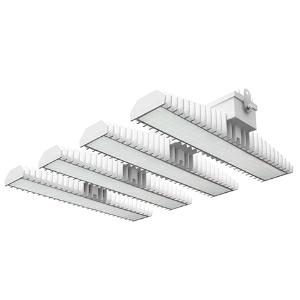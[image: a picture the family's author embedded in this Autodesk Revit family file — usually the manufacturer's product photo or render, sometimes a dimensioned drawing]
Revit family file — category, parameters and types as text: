
# Revit family: 3f_filippi_-_3f_lem_ho_ampio_3f_filippi_-_58956_a0812_-_3f_lem_4_ho_led_280_cr_ampio___vs_26d4
name_source: partatom
category: Lighting Fixtures
units: mm (PartAtom-declared; Revit-internal decimal feet)

## family parameters
Cut with Voids When Loaded = No
Host = Face
Light Source = No
Part Type = Normal
Room Calculation Point = No
Round Connector Dimension = Use Diameter
Shared = No

## types (1)
- 3F Filippi - 3F LEM HO Ampio (1 x LED, 35405 lm, 276 W, 4000 K)
    Apparent Load = 276 VA
    Approval mark = CE
    CIE Flux Codes = 67 90 97 100 100
    Color Rendering = 80
    Color Temperature = 4000 K
    Control Gear = Electronic ballast
    Default Elevation = 1800 mm
    Description = Industrial luminaire with high light output and high luminous efficiency designed with the most innovative technologies for environments with temperature up to 55°C.

ILLUMINOTECHNICAL
Luminous efficiency 100% (DLOR 98%, ULOR 2%).
Initial luminous flux of the luminaire 35405 lm.
Direct symmetric wide distribution: the illuminated area has a rectangular shape.
Installation Interdistance Transv.D = 1.24 x hu - Long.D = 1.20 x hu.
Tabular UGR (CIE 117 - 4H-8H; S=0.25H; 70/50/20): RUG 23.8 - 23.9.
Beam angle: 82° - 83°.
Luminous efficacy 128 lm/W.
Lifetime (L93/B10): 30000 h. (tq+25°C)
Lifetime (L90/B10): 50000 h. (tq+25°C)
Lifetime (L85/B10): 80000 h. (tq+25°C)
Lifetime (L80/B10): 100000 h. (tq+25°C)
Lifetime (L85/B10): 50000 h. (tq+55°C)
Sudden decreased luminous flux after 50000 hours: 0% (C0).
Photobiological safety in compliance with IEC/TR 62778: RG0 risk exempt, (IEC 62471).
In compliance with IEC/EN 62722-2-1 - IEC/EN 62717 standards.

SOURCE
4 Mid-Power linear LED modules 70W/840.
Energy efficiency class (UE 2019/2020 - UE 2019/2015): C.
CIE 13.3 Colour rendering index: CRI >80 (R9 <50%).
IES TM-30 Fidelity Index: Rf = 84 Rg = 95.
CCT nominal colour temperature 4000 K.
Colour initial tolerance (MacAdam): SDCM 3.

MECHANICAL
Passive modular heatsinks in die-casted aluminium, painted in white colour.
To optimize the thermal management of the LED module, the heatsinks are oversized and provided with self-cleaning of cooling fins.
Wiring body in aluminium and galvanised steel anchored solidly to the sinks and thermally separated.
3F Lens lenses with high luminous efficiency, transparent methacrylate (PMMA), fixed to the LED modules.
Fixing brackets in stainless steel.
Luminaire with limited surface temperature. - D - (EN 60598-2-24)
Dimensions: 757x542 mm, height 133 mm. Weight 19.325 kg.
IP65 protection degree.
Mechanical strength to impacts IK06 (1 joule).
Glow-wire test resistance 650°C.

ELECTRICAL
Halogen Free electronic wiring 230V-50/60Hz, power factor 0.97, THD <25%, constant output current, class I, 2 driver.
Power of the luminaire 276 W.
ENEC - CE.
SAFE FLICKER: PstLM=<1 and SVM=<0.4 (IEC TR 61547-1 and IEC TR 63158), to ensure a more comfortable and safe light.
Luminaire compliant with EN 60598-2-22 for power supply from a centralised emergency system CPSS (Central Power Supply System), not incorporated in the luminaire - high risk areas excluded. The default power and flux are 100% in AC and 100% in DC.
Ambient temperature from -30°C to +55°C.
Temperature class T6 max 85°C.
Quick connection via M20 3P connector with 9-13 mm tightening range.
Power unit positioned on a separate compartment by the LED module to ensure optimum temperatures of cabling components, to be inspectable and maintainable.
Relative humidity UR: <85%.

INSTALLATION
Ceiling / Suspended / Wall.
All accessories dedicated to this product are available on the Catalog and on our website www.3F-Filippi.com.

ACCESSORIES
A0812 - Anti-glare microprismatic VS moulded glass, tempered, not flammable, with sealing gasket.
One required for each light module. The pack contains 10 pieces.

APPLICATIONS
In commercial environments, exhibition and industrial areas, stores, open areas.
Environments in which it is necessary a total protection against falling fragments (eg environments with foodstuffs or machines with moving parts or with extreme temperature changes), use luminaires with polycarbonate lenses.

WARNING
Fixture not suitable for cold stores with an ambient temperature <0°C and/or relative humidity >85%.
Luminaire designed for disposal/recycling at end-of-life.
Replaceable (LED only) light source by a professional. Replaceable control gear by a professional.
    Height = 133 mm  [stored 0.436352 ft]
    Lamp = 1 x LED
    Lamp Light Flux = 35405 lm
    Lamp Power = 276 W
    Lamp count = 1
    Length = 757 mm
    Lifetime = 50000 h
    Luminous efficacy = 128 lm/W
    Manufacturer = 3F Filippi
    ModVariant = No
    Model = 3F Filippi - 58956+A0812 - 3F LEM 4 HO LED 280 CR AMPIO + VS
    Mounting Place = Ceiling
    Mounting Type = Pendant
    Number of Poles = 1
    OnlyDefault = Yes
    Power Factor = 1
    Product Name = 3F Filippi - 3F LEM HO Ampio
    Product group = pendant luminaire
    ProductGroupID = 9
    Protection Class = Protection class I
    Protection Degree = IP 65
    RLX_Detail_Level = 1
    RLX_Emergency_Light_Flux = 0 lm
    RLX_Emergency_Type = 0
    RLX_Emergency_Type_DB = No
    RlxData = <blob elided: 120349 chars, md5=bd78b871>
    Socket = socket
    Standby Power = 0 W
    System Light Flux = 35405 lm
    System Power = 276 W
    Type Comments = Product without accessories
    Type Image = 3f_filippi_-_lem_4__a0812.jpg
    URL = http://relux.com
    VarID = ---
    Voltage = 0 V
    Weight = 0.00 kg
    Width = 542 mm

note: [stored X ft] marks values corroborated as IEEE doubles in the binary element streams (Revit-internal decimal feet)

## geometry (parser evidence)
native form markers: Blend x4, Sweep x12
no freeform markers — native parametric forms only
